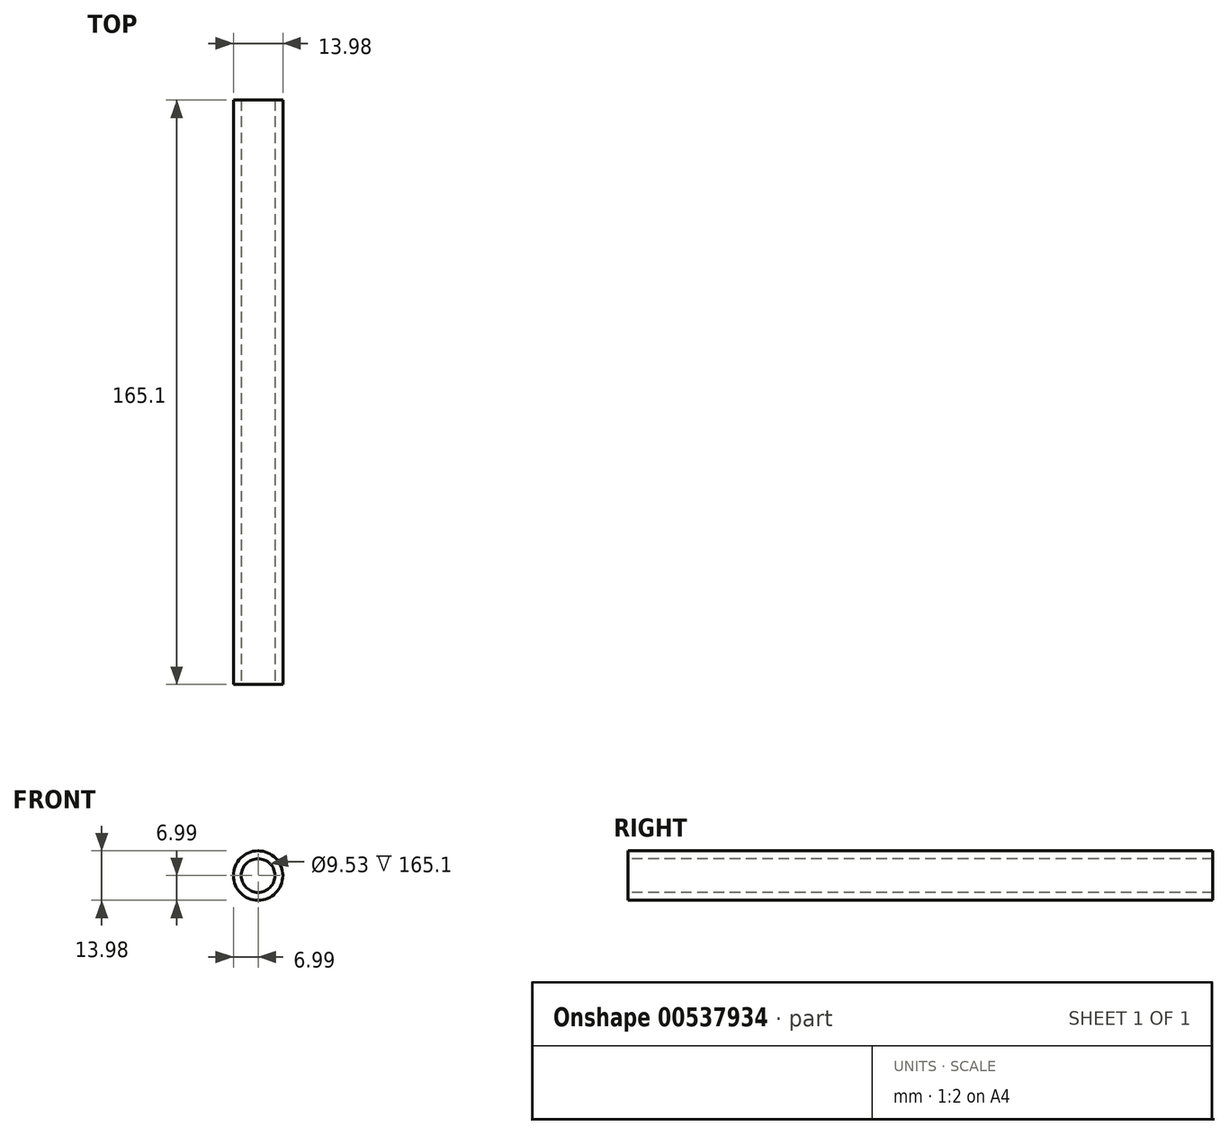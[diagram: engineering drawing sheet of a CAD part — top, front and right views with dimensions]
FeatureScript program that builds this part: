
annotation { "Feature Type Name" : "Feature", "Feature Type Description" : "" }
export const myFeature = defineFeature(function(context is Context, id is Id, definition is map)
    precondition{}
    {
        {
            var Q0;
            Q0=qCreatedBy(makeId("Front.planeOp"),FACE);
            var sketch = newSketch(context, id + "F0", { "sketchPlane" : qUnion([Q0])});
            skCircle(sketch, "E0", {"center": v(0, 0) * mm, "radius": 6.99 * mm});
            skCircle(sketch, "E1", {"center": v(0, 0) * mm, "radius": 4.76 * mm});
            skSolve(sketch);
        }
        {
            var Q0;
            Q0 = qSketchRegion(id + "F0", true);
            extrude(context, id + "F1", {"entities" : qUnion([Q0]), "oppositeDirection" : true, "depth" : 165.1 * mm, "offsetDistance" : 25.4 * mm});
        }
    });
